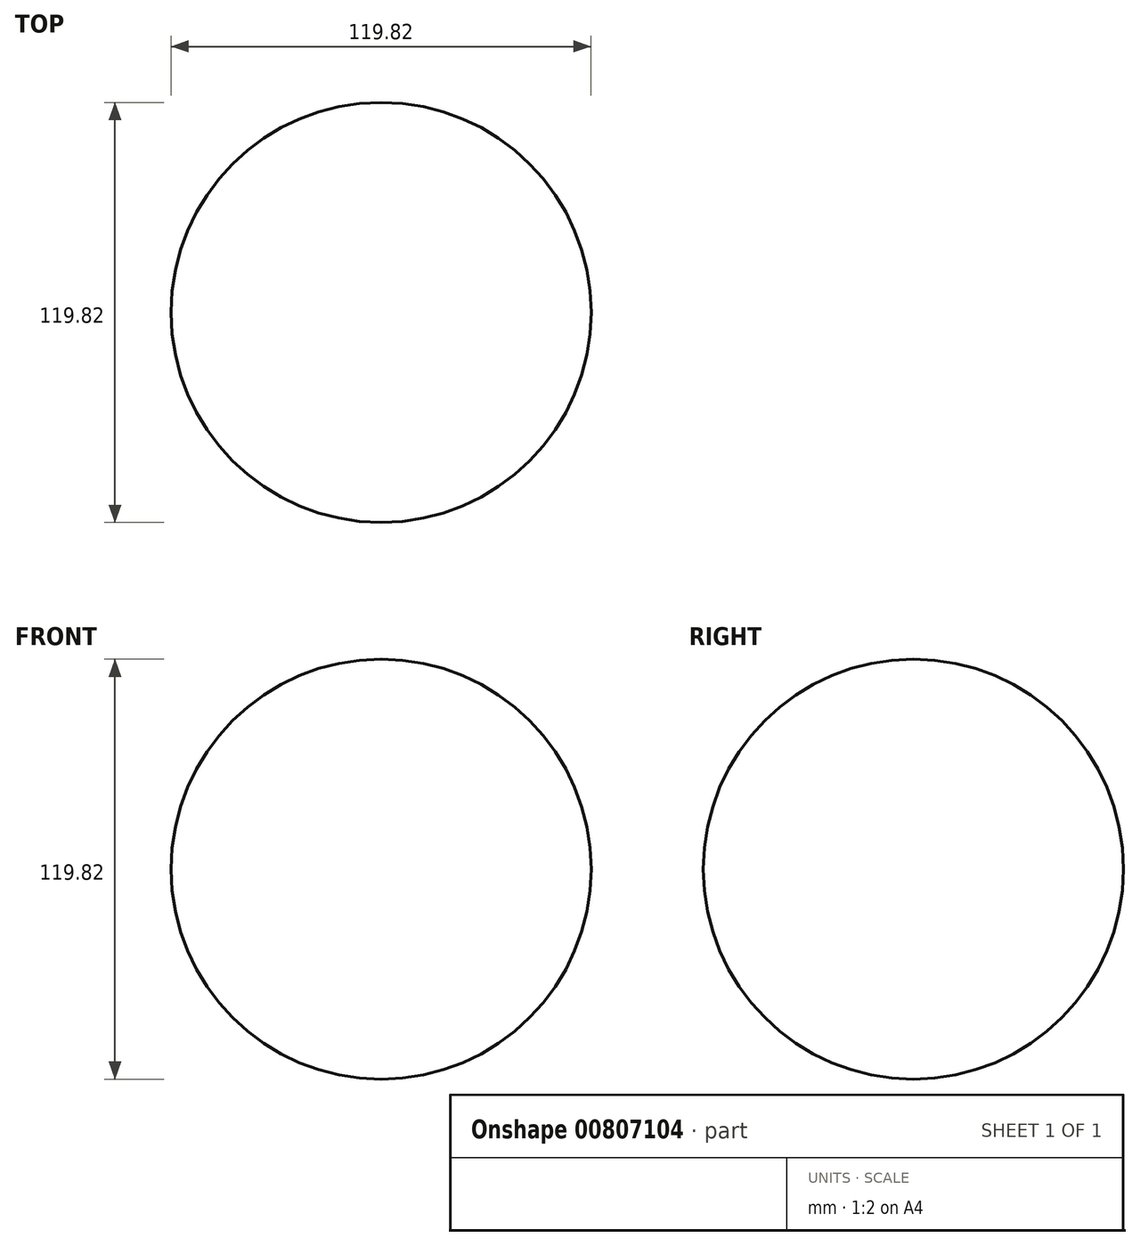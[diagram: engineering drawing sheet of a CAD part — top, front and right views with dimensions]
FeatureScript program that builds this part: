
annotation { "Feature Type Name" : "Feature", "Feature Type Description" : "" }
export const myFeature = defineFeature(function(context is Context, id is Id, definition is map)
    precondition{}
    {
        {
            var Q0;
            Q0=qCreatedBy(makeId("Front.planeOp"),FACE);
            var sketch = newSketch(context, id + "F0", { "sketchPlane" : qUnion([Q0])});
            skCircle(sketch, "E0", {"center": v(0, 0) * mm, "radius": 59.91 * mm});
            skLineSegment(sketch, "E1", {"start": v(0, 95.82) * mm, "end": v(0, -102.6) * mm});
            skSolve(sketch);
        }
        {
            var Q0;
            {var subQ0=sQuery(id+"F0.wireOp",EDGE,"E1");var subQ1=sQuery(id+"F0.wireOp",EDGE,"E0");var subQ2=makeQuery(id+"F0.imprint","INTERSECT",VERTEX,{"disambiguationData":[OD(0.0)],"derivedFrom":[subQ1,subQ0]});Q0=makeQuery(id+"F0.imprint","IMPRINT",FACE,{"disambiguationData":[TD([[makeQuery(id+"F0.imprint","IMPRINT",EDGE,{"disambiguationData":[TD([[subQ2,-1.0]])],"derivedFrom":subQ1}),1.0]])]});}
            var Q1;
            Q1=sQuery(id+"F0.wireOp",EDGE,"E1");
            revolve(context, id + "F1", {"surfaceOperationType" : NewSurfaceOperationType.NEW, "entities" : qUnion([Q0]), "axis" : qUnion([Q1]), "revolveType" : RevolveType.FULL});
        }
    });
